# Revit family: Gleitlager T, schallgedämmt, Ø20 bis 60mm
name_source: partatom
category: HLS-Bauteile
revit_build: Autodesk Revit 2018 (Build: 20190510_1515(x64)
units: mm (PartAtom-declared; Revit-internal decimal feet)

## family parameters
Arbeitsebenenbasiert = Ja
Beim Laden mit Abzugskörper schneiden = Nein
Bemaßung runder Anschluss = Durchmesser verwenden
Gemeinsam genutzt = Ja
Immer vertikal = Nein
Klassifizierung = Keine
Raumberechnungspunkt = Nein
Teiletyp = Normal

## types (9) — shared parameters
Baustoffklasse = B2
Breite Schellenband = 35 mm
Breite Unterbau = 100 mm
Dämmstärke = 6 mm  [stored 0.019685 ft]
Fabrikat = MEFA
Hersteller = MEFA
Höhe Unterbau = 110 mm
Kurztext1 = Gleitlager T h=110 35 x 4 mm
Länge Unterbau = 250 mm
Mengeneinheit = St
Schalldämmeinlage = Gummi EPDM
Sicherheitsfaktor = 1.54
Verschluss-Schraube = M10
Vorgabe-Ansicht = 1219 mm
max. Temperaturbeständigkeit = 100 °C
vpe = 1
zero-valued in all types: Stärke

## per-type parameters (varying)
| type | Artikelnummer | EAN | Gewicht | Kurztext2 | RS Titan Ø20 bis 60mm | max. Rohraußendurchmesser | min. Rohraußendurchmesser |
| Gleitlager T Ø  20-22, Gummi | 145fb0022 | 4250928460035 | 5.12 kg | 20 - 22 mm EPDM fsv | Rohrschelle Titan HD, o.A., Gummi 30Grad,Ø22 bis 60mm : Titan HD, o.A, Ø20-22, Gummi | 22 mm  [stored 0.0721785 ft] | 20 mm  [stored 0.0656168 ft] |
| Gleitlager T Ø  25, Gummi | 145fb0025 | 4250928460042 | 5.15 kg | 25 mm EPDM fsv | Rohrschelle Titan HD, o.A., Gummi 30Grad,Ø22 bis 60mm : Titan HD, o.A, Ø25, Gummi | 0 mm  [stored 0 ft] | 0 mm  [stored 0 ft] |
| Gleitlager T Ø  27-28, Gummi | 145fb0028 | 4250928460059 | 5.18 kg | 27 - 28 mm EPDM fsv | Rohrschelle Titan HD, o.A., Gummi 30Grad,Ø22 bis 60mm : Titan HD, o.A, Ø27-28, Gummi | 28 mm  [stored 0.0918635 ft] | 27 mm  [stored 0.0885827 ft] |
| Gleitlager T Ø  32, Gummi | 145fb0032 | 4250928460066 | 5.22 kg | 32 mm EPDM fsv | Rohrschelle Titan HD, o.A., Gummi 30Grad,Ø22 bis 60mm : Titan HD, o.A, Ø32, Gummi | 0 mm  [stored 0 ft] | 0 mm  [stored 0 ft] |
| Gleitlager T Ø  33-35, Gummi | 145fb0035 | 4250928460073 | 5.25 kg | 33 - 35 mm EPDM fsv | Rohrschelle Titan HD, o.A., Gummi 30Grad,Ø22 bis 60mm : Titan HD, o.A, Ø33-35, Gummi | 35 mm  [stored 0.114829 ft] | 33 mm  [stored 0.108268 ft] |
| Gleitlager T Ø  40-42, Gummi | 145fb0042 | 4250928460080 | 5.32 kg | 40 - 42 mm EPDM fsv | Rohrschelle Titan HD, o.A., Gummi 30Grad,Ø22 bis 60mm : Titan HD, o.A, Ø40-42, Gummi | 42 mm  [stored 0.137795 ft] | 40 mm  [stored 0.131234 ft] |
| Gleitlager T Ø  48-50, Gummi | 145fb0050 | 4250928460097 | 5.39 kg | 48 - 50 mm EPDM fsv | Rohrschelle Titan HD, o.A., Gummi 30Grad,Ø22 bis 60mm : Titan HD, o.A, Ø48-50, Gummi | 50 mm  [stored 0.164042 ft] | 48 mm  [stored 0.15748 ft] |
| Gleitlager T Ø  54, Gummi | 145fb0054 | 4250928460103 | 5.43 kg | 54 mm EPDM fsv | Rohrschelle Titan HD, o.A., Gummi 30Grad,Ø22 bis 60mm : Titan HD, o.A, Ø54, Gummi | 0 mm  [stored 0 ft] | 0 mm  [stored 0 ft] |
| Gleitlager T Ø  60, Gummi | 145fb0060 | 4250928460110 | 5.49 kg | 60 mm EPDM fsv | Rohrschelle Titan HD, o.A., Gummi 30Grad,Ø22 bis 60mm : Titan HD, o.A, Ø60, Gummi | 0 mm  [stored 0 ft] | 0 mm  [stored 0 ft] |

note: [stored X ft] marks values corroborated as IEEE doubles in the binary element streams (Revit-internal decimal feet)

## geometry (parser evidence)
native form markers: Sweep x8
no freeform markers — native parametric forms only
